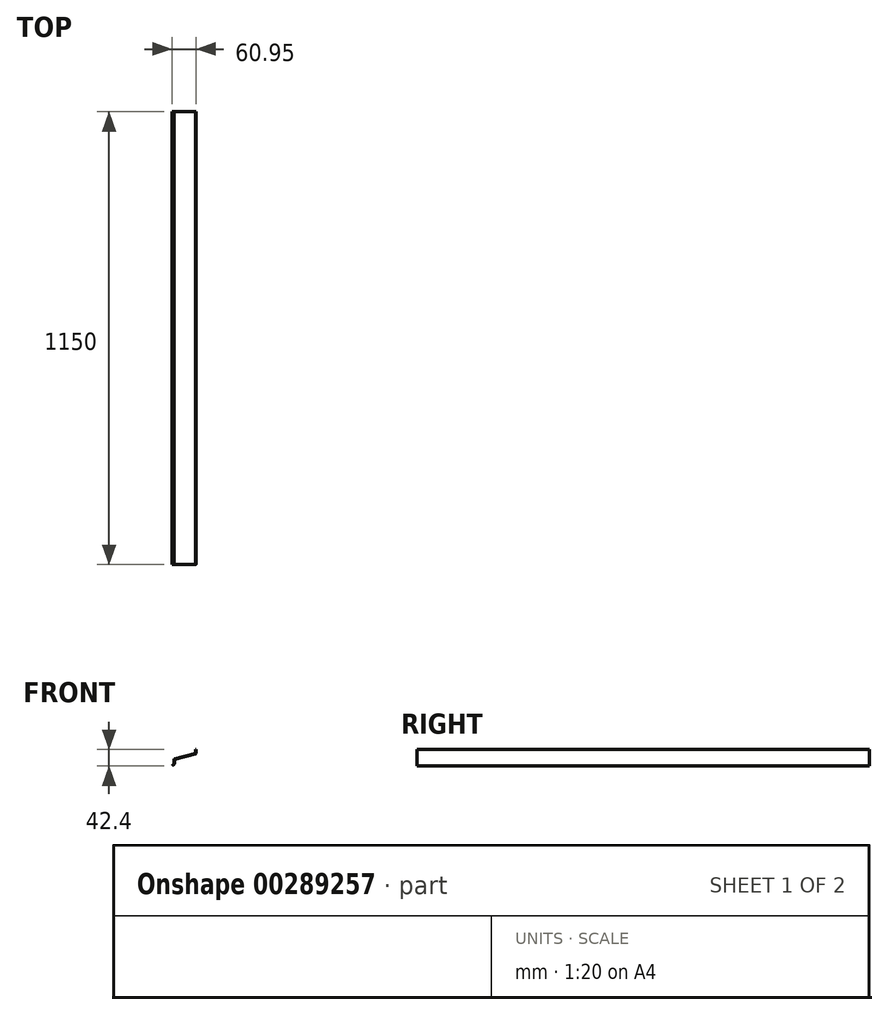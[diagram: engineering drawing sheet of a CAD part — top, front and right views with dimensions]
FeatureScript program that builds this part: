
annotation { "Feature Type Name" : "Feature", "Feature Type Description" : "" }
export const myFeature = defineFeature(function(context is Context, id is Id, definition is map)
    precondition{}
    {
        {
            var Q0;
            Q0=qCreatedBy(makeId("Front.planeOp"),FACE);
            var sketch = newSketch(context, id + "F0", { "sketchPlane" : qUnion([Q0])});
            skLineSegment(sketch, "E0", {"start": v(1.19, 0.32) * mm, "end": v(54.56, 14.62) * mm});
            skLineSegment(sketch, "E1", {"start": v(55, 15.2) * mm, "end": v(55, 24.74) * mm});
            skLineSegment(sketch, "E2", {"start": v(0, -1.23) * mm, "end": v(0, -11.75) * mm});
            skLineSegment(sketch, "E3", {"start": v(-0.18, -12.18) * mm, "end": v(-4.95, -16.95) * mm});
            skLineSegment(sketch, "E4", {"start": v(-4.95, -16.95) * mm, "end": v(-4.24, -17.66) * mm});
            skLineSegment(sketch, "E5", {"start": v(-4.24, -17.66) * mm, "end": v(0.53, -12.88) * mm});
            skLineSegment(sketch, "E6", {"start": v(1, -11.75) * mm, "end": v(1, -1.23) * mm});
            skLineSegment(sketch, "E7", {"start": v(1.44, -0.65) * mm, "end": v(54.81, 13.65) * mm});
            skLineSegment(sketch, "E8", {"start": v(56, 15.2) * mm, "end": v(56, 24.74) * mm});
            skPoint(sketch, "E9.visualSharp", {"position": v(0, -12) * mm});
            skArc(sketch, "E9.filletArc", {"start": v(-0.18, -12.18) * mm, "mid": v(-0.05, -11.98) * mm, "end": v(0, -11.75) * mm});
            skPoint(sketch, "E10.visualSharp", {"position": v(1, -0.77) * mm});
            skArc(sketch, "E10.filletArc", {"start": v(1.44, -0.65) * mm, "mid": v(1.12, -0.86) * mm, "end": v(1, -1.23) * mm});
            skPoint(sketch, "E11.visualSharp", {"position": v(55, 14.74) * mm});
            skArc(sketch, "E11.filletArc", {"start": v(54.56, 14.62) * mm, "mid": v(54.88, 14.83) * mm, "end": v(55, 15.2) * mm});
            skPoint(sketch, "E12.visualSharp", {"position": v(56, 13.97) * mm});
            skArc(sketch, "E12.filletArc", {"start": v(54.81, 13.65) * mm, "mid": v(55.67, 14.22) * mm, "end": v(56, 15.2) * mm});
            skPoint(sketch, "E13.visualSharp", {"position": v(0, 0) * mm});
            skArc(sketch, "E13.filletArc", {"start": v(1.19, 0.32) * mm, "mid": v(0.33, -0.25) * mm, "end": v(0, -1.23) * mm});
            skPoint(sketch, "E14.visualSharp", {"position": v(1, -12.41) * mm});
            skArc(sketch, "E14.filletArc", {"start": v(0.53, -12.88) * mm, "mid": v(0.88, -12.36) * mm, "end": v(1, -11.75) * mm});
            skLineSegment(sketch, "E15", {"start": v(56, 24.74) * mm, "end": v(55, 24.74) * mm});
            skSolve(sketch);
        }
        {
            var Q0;
            Q0=makeQuery(id+"F0.imprint","IMPRINT",FACE,{"disambiguationData":[TD([[makeQuery(id+"F0.imprint","IMPRINT",EDGE,{"derivedFrom":sQuery(id+"F0.wireOp",EDGE,"E0")}),-1.0]])]});
            extrude(context, id + "F1", {"entities" : qUnion([Q0]), "endBound" : BoundingType.SYMMETRIC, "depth" : 1150 * mm});
        }
    });
